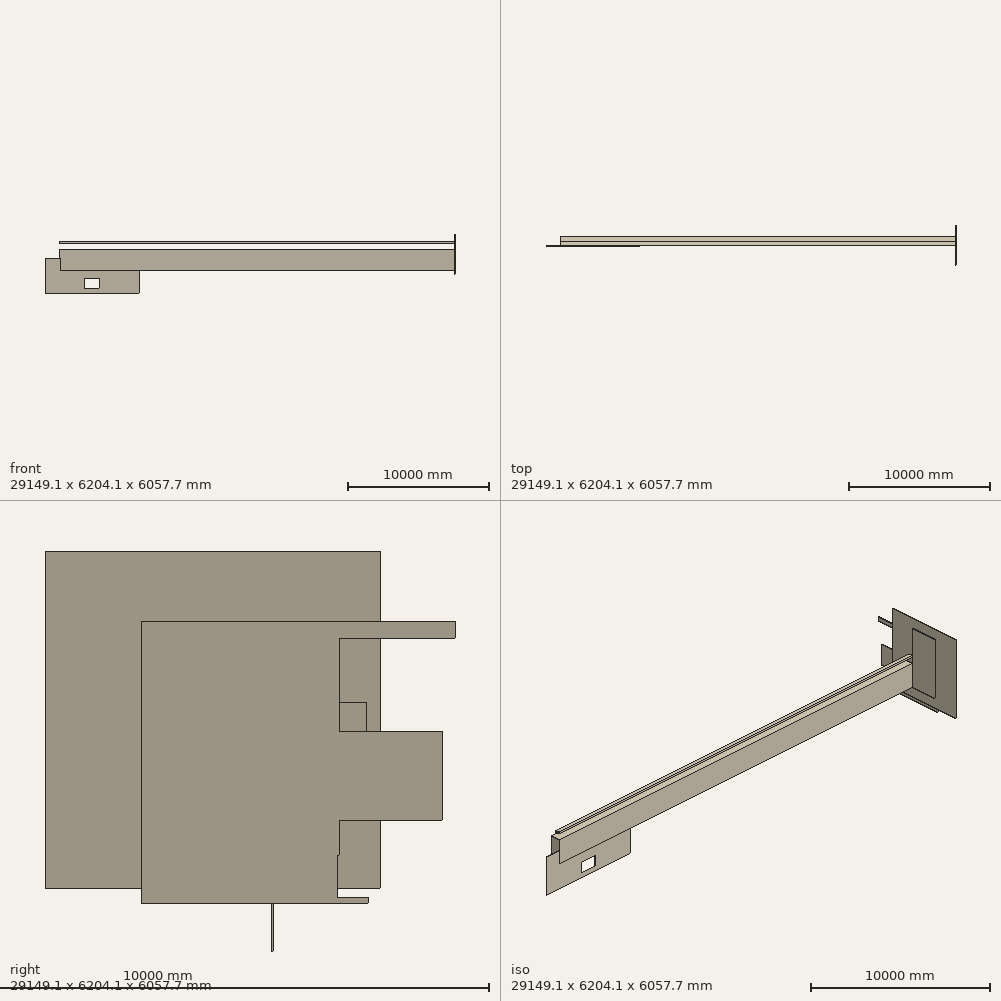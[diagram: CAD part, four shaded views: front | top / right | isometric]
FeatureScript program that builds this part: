
annotation { "Feature Type Name" : "Feature", "Feature Type Description" : "" }
export const myFeature = defineFeature(function(context is Context, id is Id, definition is map)
    precondition{}
    {
        {
            var Q0;
            Q0=qCreatedBy(makeId("Right.planeOp"),FACE);
            var sketch = newSketch(context, id + "F0", { "sketchPlane" : qUnion([Q0])});
            skLineSegment(sketch, "E0.bottom", {"start": v(750.29, 608.07) * mm, "end": v(-916.02, 608.07) * mm});
            skLineSegment(sketch, "E0.top", {"start": v(750.29, -832.28) * mm, "end": v(-916.02, -832.28) * mm});
            skLineSegment(sketch, "E0.left", {"start": v(750.29, 608.07) * mm, "end": v(750.29, -832.28) * mm});
            skLineSegment(sketch, "E0.right", {"start": v(-916.02, 608.07) * mm, "end": v(-916.02, -832.28) * mm});
            skLineSegment(sketch, "E1.bottom", {"start": v(0, 0) * mm, "end": v(321.95, 0) * mm});
            skLineSegment(sketch, "E1.top", {"start": v(0, 173.87) * mm, "end": v(321.95, 173.87) * mm});
            skLineSegment(sketch, "E1.left", {"start": v(0, 0) * mm, "end": v(0, 173.87) * mm});
            skLineSegment(sketch, "E1.right", {"start": v(321.95, 0) * mm, "end": v(321.95, 173.87) * mm});
            skSolve(sketch);
        }
        {
            var Q0;
            Q0 = qSketchRegion(id + "F0", true);
            extrude(context, id + "F1", {"entities" : qUnion([Q0]), "depth" : 25.4 * mm, "offsetDistance" : 25.4 * mm});
        }
        {
            var Q0;
            Q0=makeQuery(id+"F1.opExtrude","CAP_FACE",FACE,{"disambiguationData":[OSD([sQuery(id+"F0.wireOp",EDGE,"E0.bottom"),sQuery(id+"F0.wireOp",EDGE,"E0.top"),sQuery(id+"F0.wireOp",EDGE,"E0.left"),sQuery(id+"F0.wireOp",EDGE,"E0.right"),sQuery(id+"F0.wireOp",EDGE,"E1.bottom"),sQuery(id+"F0.wireOp",EDGE,"E1.top"),sQuery(id+"F0.wireOp",EDGE,"E1.left"),sQuery(id+"F0.wireOp",EDGE,"E1.right")])],"isStart":false});
            var sketch = newSketch(context, id + "F2", { "sketchPlane" : qUnion([Q0])});
            skLineSegment(sketch, "E2.bottom", {"start": v(901.92, -1092.77) * mm, "end": v(-1059.43, -1092.77) * mm});
            skLineSegment(sketch, "E2.top", {"start": v(901.92, 856.03) * mm, "end": v(-1059.43, 856.03) * mm});
            skLineSegment(sketch, "E2.left", {"start": v(901.92, -1092.77) * mm, "end": v(901.92, 856.03) * mm});
            skLineSegment(sketch, "E2.right", {"start": v(-1059.43, -1092.77) * mm, "end": v(-1059.43, 856.03) * mm});
            skLineSegment(sketch, "E3.bottom", {"start": v(901.92, -524.16) * mm, "end": v(1412.93, -524.16) * mm});
            skLineSegment(sketch, "E3.top", {"start": v(901.92, 428.57) * mm, "end": v(1412.93, 428.57) * mm});
            skLineSegment(sketch, "E3.left", {"start": v(901.92, -524.16) * mm, "end": v(901.92, 428.57) * mm});
            skLineSegment(sketch, "E3.right", {"start": v(1412.93, -524.16) * mm, "end": v(1412.93, 428.57) * mm});
            skLineSegment(sketch, "E4.bottom", {"start": v(-642.52, 940.94) * mm, "end": v(927.99, 940.94) * mm});
            skLineSegment(sketch, "E4.top", {"start": v(-642.52, 1309.7) * mm, "end": v(927.99, 1309.7) * mm});
            skLineSegment(sketch, "E4.left", {"start": v(-642.52, 940.94) * mm, "end": v(-642.52, 1309.7) * mm});
            skLineSegment(sketch, "E4.right", {"start": v(927.99, 940.94) * mm, "end": v(927.99, 1309.7) * mm});
            skLineSegment(sketch, "E5.bottom", {"start": v(927.99, 940.94) * mm, "end": v(1412.93, 940.94) * mm});
            skLineSegment(sketch, "E5.top", {"start": v(927.99, 428.57) * mm, "end": v(1412.93, 428.57) * mm});
            skLineSegment(sketch, "E5.left", {"start": v(927.99, 940.94) * mm, "end": v(927.99, 428.57) * mm});
            skLineSegment(sketch, "E5.right", {"start": v(1412.93, 940.94) * mm, "end": v(1412.93, 428.57) * mm});
            skLineSegment(sketch, "E6.bottom", {"start": v(-642.52, 1006.43) * mm, "end": v(-1059.43, 1006.43) * mm});
            skLineSegment(sketch, "E6.top", {"start": v(-642.52, 856.03) * mm, "end": v(-1059.43, 856.03) * mm});
            skLineSegment(sketch, "E6.left", {"start": v(-642.52, 1006.43) * mm, "end": v(-642.52, 856.03) * mm});
            skLineSegment(sketch, "E6.right", {"start": v(-1059.43, 1006.43) * mm, "end": v(-1059.43, 856.03) * mm});
            skLineSegment(sketch, "E7.bottom", {"start": v(601.3, -1092.77) * mm, "end": v(0, -1092.77) * mm});
            skLineSegment(sketch, "E7.top", {"start": v(601.3, -1363.04) * mm, "end": v(0, -1363.04) * mm});
            skLineSegment(sketch, "E7.left", {"start": v(601.3, -1092.77) * mm, "end": v(601.3, -1363.04) * mm});
            skLineSegment(sketch, "E7.right", {"start": v(0, -1092.77) * mm, "end": v(0, -1363.04) * mm});
            skLineSegment(sketch, "E8.bottom", {"start": v(-484.82, -1092.77) * mm, "end": v(-1031.03, -1092.77) * mm});
            skLineSegment(sketch, "E8.top", {"start": v(-484.82, -1486.2) * mm, "end": v(-1031.03, -1486.2) * mm});
            skLineSegment(sketch, "E8.left", {"start": v(-484.82, -1092.77) * mm, "end": v(-484.82, -1486.2) * mm});
            skLineSegment(sketch, "E8.right", {"start": v(-1031.03, -1092.77) * mm, "end": v(-1031.03, -1486.2) * mm});
            skLineSegment(sketch, "E9.bottom", {"start": v(-1059.43, -688.86) * mm, "end": v(-1375.11, -688.86) * mm});
            skLineSegment(sketch, "E9.top", {"start": v(-1059.43, -191.77) * mm, "end": v(-1375.11, -191.77) * mm});
            skLineSegment(sketch, "E9.left", {"start": v(-1059.43, -688.86) * mm, "end": v(-1059.43, -191.77) * mm});
            skLineSegment(sketch, "E9.right", {"start": v(-1375.11, -688.86) * mm, "end": v(-1375.11, -191.77) * mm});
            skLineSegment(sketch, "E10.bottom", {"start": v(-1059.43, 243.74) * mm, "end": v(-1322.9, 243.74) * mm});
            skLineSegment(sketch, "E10.top", {"start": v(-1059.43, 658.68) * mm, "end": v(-1322.9, 658.68) * mm});
            skLineSegment(sketch, "E10.left", {"start": v(-1059.43, 243.74) * mm, "end": v(-1059.43, 658.68) * mm});
            skLineSegment(sketch, "E10.right", {"start": v(-1322.9, 243.74) * mm, "end": v(-1322.9, 658.68) * mm});
            skSolve(sketch);
        }
        {
            var Q0;
            Q0 = qSketchRegion(id + "F2", true);
            extrude(context, id + "F3", {"entities" : qUnion([Q0]), "operationType" : NewBodyOperationType.ADD, "depth" : 25.4 * mm, "offsetDistance" : 25.4 * mm});
        }
        {
            var Q0;
            Q0=makeQuery(id+"F1.opExtrude","CAP_FACE",FACE,{"disambiguationData":[OSD([sQuery(id+"F0.wireOp",EDGE,"E0.bottom"),sQuery(id+"F0.wireOp",EDGE,"E0.top"),sQuery(id+"F0.wireOp",EDGE,"E0.left"),sQuery(id+"F0.wireOp",EDGE,"E0.right"),sQuery(id+"F0.wireOp",EDGE,"E1.bottom"),sQuery(id+"F0.wireOp",EDGE,"E1.top"),sQuery(id+"F0.wireOp",EDGE,"E1.left"),sQuery(id+"F0.wireOp",EDGE,"E1.right")])],"isStart":true});
            var sketch = newSketch(context, id + "F4", { "sketchPlane" : qUnion([Q0])});
            skLineSegment(sketch, "E11.bottom", {"start": v(0, -1222.01) * mm, "end": v(1832.05, -1222.01) * mm});
            skLineSegment(sketch, "E11.top", {"start": v(0, 2585.08) * mm, "end": v(1832.05, 2585.08) * mm});
            skLineSegment(sketch, "E11.left", {"start": v(0, -1222.01) * mm, "end": v(0, 2585.08) * mm});
            skLineSegment(sketch, "E11.right", {"start": v(1832.05, -1222.01) * mm, "end": v(1832.05, 2585.08) * mm});
            skPoint(sketch, "E11.middle", {"position": v(916.02, 681.54) * mm});
            skSolve(sketch);
        }
        {
            var Q0;
            Q0 = qSketchRegion(id + "F4", true);
            extrude(context, id + "F5", {"entities" : qUnion([Q0]), "operationType" : NewBodyOperationType.ADD, "depth" : 25.4 * mm, "offsetDistance" : 25.4 * mm});
        }
        {
            var Q0;
            {var subQ0=sQuery(id+"F2.wireOp",EDGE,"E7.right");var subQ1=sQuery(id+"F2.wireOp",EDGE,"E7.left");var subQ2=sQuery(id+"F2.wireOp",EDGE,"E7.top");var subQ3=sQuery(id+"F2.wireOp",EDGE,"E6.bottom");var subQ4=sQuery(id+"F2.wireOp",EDGE,"E5.bottom");var subQ5=sQuery(id+"F2.wireOp",EDGE,"E4.right");var subQ6=sQuery(id+"F2.wireOp",EDGE,"E4.left");var subQ7=sQuery(id+"F2.wireOp",EDGE,"E4.top");var subQ8=sQuery(id+"F2.wireOp",EDGE,"E5.right");var subQ9=sQuery(id+"F2.wireOp",EDGE,"E3.right");var subQ10=sQuery(id+"F2.wireOp",EDGE,"E3.bottom");var subQ11=sQuery(id+"F2.wireOp",EDGE,"E6.right");var subQ12=sQuery(id+"F2.wireOp",EDGE,"E2.right");var subQ14=sQuery(id+"F2.wireOp",EDGE,"E2.bottom");var subQ15=sQuery(id+"F2.wireOp",EDGE,"E8.left");var subQ17=sQuery(id+"F2.wireOp",EDGE,"E9.bottom");var subQ18=sQuery(id+"F2.wireOp",EDGE,"E9.right");var subQ20=sQuery(id+"F2.wireOp",EDGE,"E8.right");var subQ21=sQuery(id+"F2.wireOp",EDGE,"E8.top");var subQ22=sQuery(id+"F2.wireOp",EDGE,"E9.top");var subQ23=sQuery(id+"F2.wireOp",EDGE,"E2.left");var subQ25=sQuery(id+"F2.wireOp",EDGE,"E10.bottom");var subQ26=sQuery(id+"F2.wireOp",EDGE,"E10.top");var subQ27=sQuery(id+"F2.wireOp",EDGE,"E10.right");Q0=makeQuery(id+"F3.boolean.opBoolean","SPLIT",FACE,{"disambiguationData":[TD([makeQuery(id+"F1.opExtrude","SWEPT_FACE",FACE,{"disambiguationData":[OSD([sQuery(id+"F0.wireOp",EDGE,"E0.bottom")])]})])],"derivedFrom":makeQuery(id+"F3.opExtrude","CAP_FACE",FACE,{"disambiguationData":[OSD([subQ14,subQ23,subQ12,subQ10,subQ9,subQ7,subQ6,subQ5,subQ4,subQ8,subQ3,subQ11,subQ2,subQ1,subQ0,subQ21,subQ15,subQ20,subQ17,subQ22,subQ18,subQ25,subQ26,subQ27])],"isStart":true})});}
            var sketch = newSketch(context, id + "F6", { "sketchPlane" : qUnion([Q0])});
            skLineSegment(sketch, "E12.bottom", {"start": v(0, -1227.9) * mm, "end": v(-670.01, -1227.9) * mm});
            skLineSegment(sketch, "E12.top", {"start": v(0, 304) * mm, "end": v(-670.01, 304) * mm});
            skLineSegment(sketch, "E12.left", {"start": v(0, -1227.9) * mm, "end": v(0, 304) * mm});
            skLineSegment(sketch, "E12.right", {"start": v(-670.01, -1227.9) * mm, "end": v(-670.01, 304) * mm});
            skLineSegment(sketch, "E13.bottom", {"start": v(0, 713.4) * mm, "end": v(-276.83, 713.4) * mm});
            skLineSegment(sketch, "E13.top", {"start": v(0, 819.68) * mm, "end": v(-276.83, 819.68) * mm});
            skLineSegment(sketch, "E13.left", {"start": v(0, 713.4) * mm, "end": v(0, 819.68) * mm});
            skLineSegment(sketch, "E13.right", {"start": v(-276.83, 713.4) * mm, "end": v(-276.83, 819.68) * mm});
            skSolve(sketch);
        }
        {
            var Q0;
            Q0 = qSketchRegion(id + "F6", true);
            extrude(context, id + "F7", {"entities" : qUnion([Q0]), "operationType" : NewBodyOperationType.ADD, "depth" : 28066.47 * mm, "offsetDistance" : 25.4 * mm});
        }
        {
            var Q0;
            Q0=makeQuery(id+"F5.opExtrude","CAP_FACE",FACE,{"disambiguationData":[OSD([sQuery(id+"F4.wireOp",EDGE,"E11.bottom"),sQuery(id+"F4.wireOp",EDGE,"E11.top"),sQuery(id+"F4.wireOp",EDGE,"E11.left"),sQuery(id+"F4.wireOp",EDGE,"E11.right")])],"isStart":true});
            var sketch = newSketch(context, id + "F8", { "sketchPlane" : qUnion([Q0])});
            skLineSegment(sketch, "E14.bottom", {"start": v(-3443.48, -1861.85) * mm, "end": v(1627.63, -1861.85) * mm});
            skLineSegment(sketch, "E14.top", {"start": v(-3443.48, 3235.6) * mm, "end": v(1627.63, 3235.6) * mm});
            skLineSegment(sketch, "E14.left", {"start": v(-3443.48, -1861.85) * mm, "end": v(-3443.48, 3235.6) * mm});
            skLineSegment(sketch, "E14.right", {"start": v(1627.63, -1861.85) * mm, "end": v(1627.63, 3235.6) * mm});
            skSolve(sketch);
        }
        {
            var Q0;
            Q0 = qSketchRegion(id + "F8", true);
            extrude(context, id + "F9", {"entities" : qUnion([Q0]), "operationType" : NewBodyOperationType.ADD, "depth" : 25.4 * mm, "offsetDistance" : 25.4 * mm});
        }
        {
            var Q0;
            {var subQ2=sQuery(id+"F0.wireOp",EDGE,"E1.left");var subQ4=sQuery(id+"F6.wireOp",EDGE,"E12.left");Q0=makeQuery(id+"F9.boolean.opBoolean","SPLIT",FACE,{"disambiguationData":[TD([makeQuery(id+"F1.opExtrude","SWEPT_FACE",FACE,{"disambiguationData":[OSD([subQ2])]})])],"derivedFrom":makeQuery(id+"F7.boolean.opBoolean","MERGE",FACE,{"derivedFrom":[makeQuery(id+"F3.opExtrude","SWEPT_FACE",FACE,{"disambiguationData":[OSD([sQuery(id+"F2.wireOp",EDGE,"E7.right")])]}),makeQuery(id+"F7.opExtrude","SWEPT_FACE",FACE,{"disambiguationData":[OSD([subQ4])]})]})});}
            var sketch = newSketch(context, id + "F10", { "sketchPlane" : qUnion([Q0])});
            skLineSegment(sketch, "E15.bottom", {"start": v(-28041.07, -1227.9) * mm, "end": v(-24540.4, -1227.9) * mm});
            skLineSegment(sketch, "E15.top", {"start": v(-28041.07, -2822.09) * mm, "end": v(-24540.4, -2822.09) * mm});
            skLineSegment(sketch, "E15.left", {"start": v(-28041.07, -1227.9) * mm, "end": v(-28041.07, -2822.09) * mm});
            skLineSegment(sketch, "E15.right", {"start": v(-24540.4, -1227.9) * mm, "end": v(-24540.4, -2822.09) * mm});
            skLineSegment(sketch, "E16.bottom", {"start": v(-24540.4, -2822.09) * mm, "end": v(-22407, -2822.09) * mm});
            skLineSegment(sketch, "E16.top", {"start": v(-24540.4, -1227.9) * mm, "end": v(-22407, -1227.9) * mm});
            skLineSegment(sketch, "E16.left", {"start": v(-24540.4, -2822.09) * mm, "end": v(-24540.4, -1227.9) * mm});
            skLineSegment(sketch, "E16.right", {"start": v(-22407, -2822.09) * mm, "end": v(-22407, -1227.9) * mm});
            skLineSegment(sketch, "E17.bottom", {"start": v(-28041.07, -2822.09) * mm, "end": v(-29072.93, -2822.09) * mm});
            skLineSegment(sketch, "E17.top", {"start": v(-28041.07, -372.62) * mm, "end": v(-29072.93, -372.62) * mm});
            skLineSegment(sketch, "E17.left", {"start": v(-28041.07, -2822.09) * mm, "end": v(-28041.07, -372.62) * mm});
            skLineSegment(sketch, "E17.right", {"start": v(-29072.93, -2822.09) * mm, "end": v(-29072.93, -372.62) * mm});
            skLineSegment(sketch, "E18.bottom", {"start": v(-28041.07, -1227.9) * mm, "end": v(-26597.95, -1227.9) * mm});
            skLineSegment(sketch, "E18.top", {"start": v(-28041.07, -2719.46) * mm, "end": v(-26597.95, -2719.46) * mm});
            skLineSegment(sketch, "E18.left", {"start": v(-28041.07, -1227.9) * mm, "end": v(-28041.07, -2719.46) * mm});
            skLineSegment(sketch, "E18.right", {"start": v(-26597.95, -1227.9) * mm, "end": v(-26597.95, -2719.46) * mm});
            skLineSegment(sketch, "E19.bottom", {"start": v(-26335.87, -2522.71) * mm, "end": v(-25226.13, -2522.71) * mm});
            skLineSegment(sketch, "E19.top", {"start": v(-26335.87, -1819.2) * mm, "end": v(-25226.13, -1819.2) * mm});
            skLineSegment(sketch, "E19.left", {"start": v(-26335.87, -2522.71) * mm, "end": v(-26335.87, -1819.2) * mm});
            skLineSegment(sketch, "E19.right", {"start": v(-25226.13, -2522.71) * mm, "end": v(-25226.13, -1819.2) * mm});
            skSolve(sketch);
        }
        {
            var Q0;
            Q0 = qSketchRegion(id + "F10", true);
            extrude(context, id + "F11", {"entities" : qUnion([Q0]), "depth" : 25.4 * mm, "offsetDistance" : 25.4 * mm});
        }
        {
            var Q0;
            Q0=makeQuery(id+"F3.opExtrude","CAP_FACE",FACE,{"disambiguationData":[OSD([sQuery(id+"F2.wireOp",EDGE,"E2.bottom"),sQuery(id+"F2.wireOp",EDGE,"E2.left"),sQuery(id+"F2.wireOp",EDGE,"E2.right"),sQuery(id+"F2.wireOp",EDGE,"E3.bottom"),sQuery(id+"F2.wireOp",EDGE,"E3.right"),sQuery(id+"F2.wireOp",EDGE,"E4.top"),sQuery(id+"F2.wireOp",EDGE,"E4.left"),sQuery(id+"F2.wireOp",EDGE,"E4.right"),sQuery(id+"F2.wireOp",EDGE,"E5.bottom"),sQuery(id+"F2.wireOp",EDGE,"E5.right"),sQuery(id+"F2.wireOp",EDGE,"E6.bottom"),sQuery(id+"F2.wireOp",EDGE,"E6.right"),sQuery(id+"F2.wireOp",EDGE,"E7.top"),sQuery(id+"F2.wireOp",EDGE,"E7.left"),sQuery(id+"F2.wireOp",EDGE,"E7.right"),sQuery(id+"F2.wireOp",EDGE,"E8.top"),sQuery(id+"F2.wireOp",EDGE,"E8.left"),sQuery(id+"F2.wireOp",EDGE,"E8.right"),sQuery(id+"F2.wireOp",EDGE,"E9.bottom"),sQuery(id+"F2.wireOp",EDGE,"E9.top"),sQuery(id+"F2.wireOp",EDGE,"E9.right"),sQuery(id+"F2.wireOp",EDGE,"E10.bottom"),sQuery(id+"F2.wireOp",EDGE,"E10.top"),sQuery(id+"F2.wireOp",EDGE,"E10.right")])],"isStart":false});
            var sketch = newSketch(context, id + "F12", { "sketchPlane" : qUnion([Q0])});
            skLineSegment(sketch, "E20.bottom", {"start": v(-1996.62, 1918.01) * mm, "end": v(2760.61, 1918.01) * mm});
            skLineSegment(sketch, "E20.top", {"start": v(-1996.62, 2172.74) * mm, "end": v(2760.61, 2172.74) * mm});
            skLineSegment(sketch, "E20.left", {"start": v(-1996.62, 1918.01) * mm, "end": v(-1996.62, 2172.74) * mm});
            skLineSegment(sketch, "E20.right", {"start": v(2760.61, 1918.01) * mm, "end": v(2760.61, 2172.74) * mm});
            skPoint(sketch, "E21.oppositeSnap0", {"position": v(-1375.11, -440.31) * mm});
            skLineSegment(sketch, "E21.bottom", {"start": v(-1996.62, 1918.01) * mm, "end": v(-1375.11, 1918.01) * mm});
            skLineSegment(sketch, "E21.top", {"start": v(-1996.62, -2097.66) * mm, "end": v(-1375.11, -2097.66) * mm});
            skLineSegment(sketch, "E21.left", {"start": v(-1996.62, 1918.01) * mm, "end": v(-1996.62, -2097.66) * mm});
            skLineSegment(sketch, "E21.right", {"start": v(-1375.11, 1918.01) * mm, "end": v(-1375.11, -2097.66) * mm});
            skLineSegment(sketch, "E22.bottom", {"start": v(1444.89, -2008.36) * mm, "end": v(-1375.11, -2008.36) * mm});
            skLineSegment(sketch, "E22.top", {"start": v(1444.89, -2097.66) * mm, "end": v(-1375.11, -2097.66) * mm});
            skLineSegment(sketch, "E22.left", {"start": v(1444.89, -2008.36) * mm, "end": v(1444.89, -2097.66) * mm});
            skLineSegment(sketch, "E22.right", {"start": v(-1375.11, -2008.36) * mm, "end": v(-1375.11, -2097.66) * mm});
            skLineSegment(sketch, "E23.bottom", {"start": v(1005.3, -1363.04) * mm, "end": v(-1375.11, -1363.04) * mm});
            skLineSegment(sketch, "E23.top", {"start": v(1005.3, 1918.01) * mm, "end": v(-1375.11, 1918.01) * mm});
            skLineSegment(sketch, "E23.left", {"start": v(1005.3, -1363.04) * mm, "end": v(1005.3, 1918.01) * mm});
            skLineSegment(sketch, "E23.right", {"start": v(-1375.11, -1363.04) * mm, "end": v(-1375.11, 1918.01) * mm});
            skLineSegment(sketch, "E24.bottom", {"start": v(-1375.11, -1363.04) * mm, "end": v(978, -1363.04) * mm});
            skLineSegment(sketch, "E24.top", {"start": v(-1375.11, -2097.66) * mm, "end": v(978, -2097.66) * mm});
            skLineSegment(sketch, "E24.left", {"start": v(-1375.11, -1363.04) * mm, "end": v(-1375.11, -2097.66) * mm});
            skLineSegment(sketch, "E24.right", {"start": v(978, -1363.04) * mm, "end": v(978, -2097.66) * mm});
            skLineSegment(sketch, "E25.bottom", {"start": v(1005.3, 507.62) * mm, "end": v(2557.42, 507.62) * mm});
            skLineSegment(sketch, "E25.top", {"start": v(1005.3, -843.8) * mm, "end": v(2557.42, -843.8) * mm});
            skLineSegment(sketch, "E25.left", {"start": v(1005.3, 507.62) * mm, "end": v(1005.3, -843.8) * mm});
            skLineSegment(sketch, "E25.right", {"start": v(2557.42, 507.62) * mm, "end": v(2557.42, -843.8) * mm});
            skSolve(sketch);
        }
        {
            var Q0;
            Q0 = qSketchRegion(id + "F12", true);
            extrude(context, id + "F13", {"entities" : qUnion([Q0]), "operationType" : NewBodyOperationType.ADD, "depth" : 25.4 * mm, "offsetDistance" : 25.4 * mm});
        }
    });
